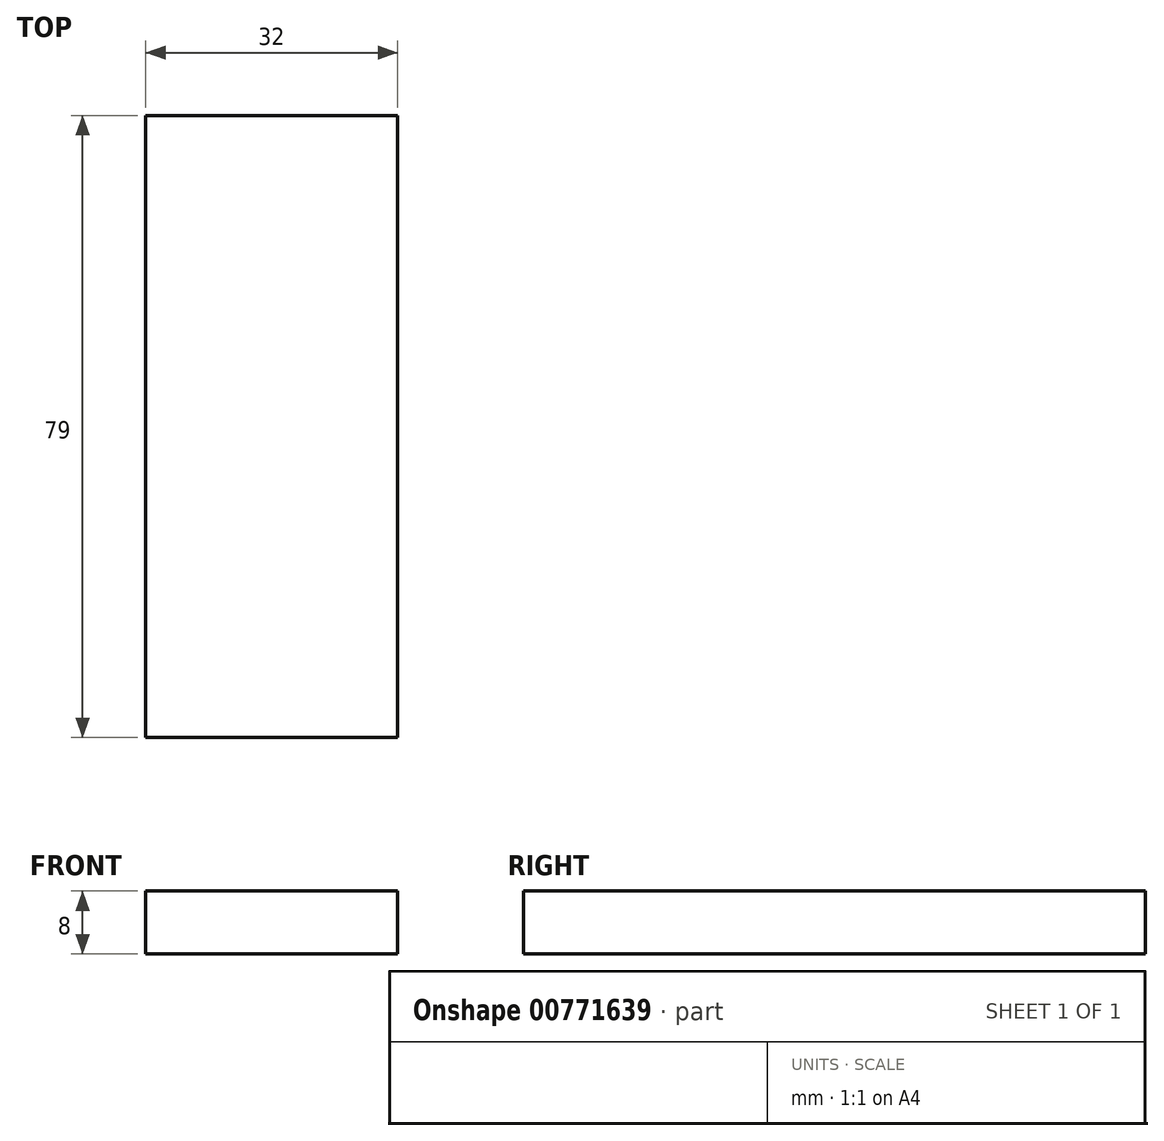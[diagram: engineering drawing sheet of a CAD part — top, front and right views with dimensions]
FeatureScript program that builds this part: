
annotation { "Feature Type Name" : "Feature", "Feature Type Description" : "" }
export const myFeature = defineFeature(function(context is Context, id is Id, definition is map)
    precondition{}
    {
        {
            var Q0;
            Q0=qCreatedBy(makeId("Top.planeOp"),FACE);
            var sketch = newSketch(context, id + "F0", { "sketchPlane" : qUnion([Q0])});
            skLineSegment(sketch, "E0.bottom", {"start": v(-31.68, 61.43) * mm, "end": v(0.32, 61.43) * mm});
            skLineSegment(sketch, "E0.top", {"start": v(-31.68, -17.57) * mm, "end": v(0.32, -17.57) * mm});
            skLineSegment(sketch, "E0.left", {"start": v(-31.68, 61.43) * mm, "end": v(-31.68, -17.57) * mm});
            skLineSegment(sketch, "E0.right", {"start": v(0.32, 61.43) * mm, "end": v(0.32, -17.57) * mm});
            skSolve(sketch);
        }
        {
            var Q0;
            Q0 = qSketchRegion(id + "F0", true);
            extrude(context, id + "F1", {"entities" : qUnion([Q0]), "depth" : 8 * mm, "offsetDistance" : 25 * mm});
        }
    });
